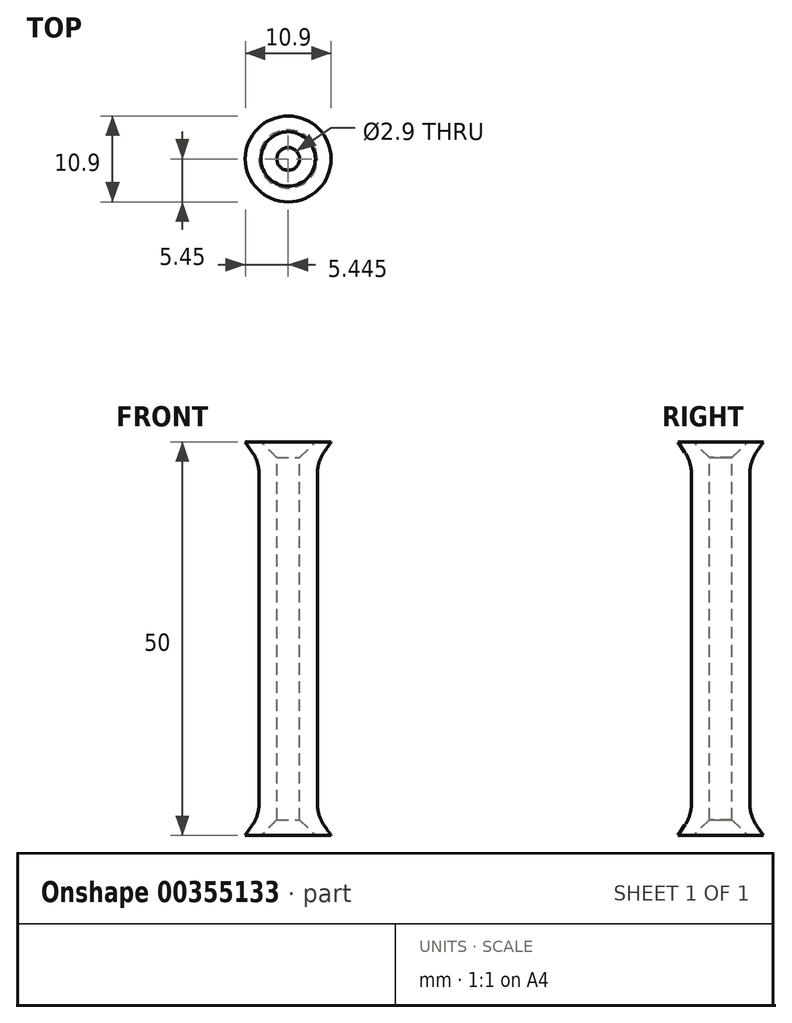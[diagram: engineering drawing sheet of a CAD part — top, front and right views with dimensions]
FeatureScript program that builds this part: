
annotation { "Feature Type Name" : "Feature", "Feature Type Description" : "" }
export const myFeature = defineFeature(function(context is Context, id is Id, definition is map)
    precondition{}
    {
        {
            var Q0;
            Q0=qCreatedBy(makeId("Front.planeOp"),FACE);
            var sketch = newSketch(context, id + "F0", { "sketchPlane" : qUnion([Q0])});
            skLineSegment(sketch, "E0", {"start": v(-17.56, 9.3) * mm, "end": v(-13.56, 9.3) * mm});
            skLineSegment(sketch, "E1", {"start": v(-13.56, 9.3) * mm, "end": v(-13.56, -15.7) * mm});
            skLineSegment(sketch, "E2", {"start": v(-13.56, -15.7) * mm, "end": v(-15.81, -15.7) * mm});
            skLineSegment(sketch, "E3", {"start": v(-15.81, -15.7) * mm, "end": v(-15.81, 6.74) * mm});
            skLineSegment(sketch, "E4", {"start": v(-15.81, 6.74) * mm, "end": v(-17.56, 9.3) * mm});
            skLineSegment(sketch, "E5", {"start": v(-12.11, -9.2) * mm, "end": v(-12.11, -18.1) * mm, "construction": true});
            skLineSegment(sketch, "E6", {"start": v(-13.56, -15.7) * mm, "end": v(-8.34, -15.7) * mm, "construction": true});
            skLineSegment(sketch, "E7.MirrorCS", {"start": v(-13.56, -40.7) * mm, "end": v(-13.56, -15.7) * mm});
            skLineSegment(sketch, "E8.MirrorCS", {"start": v(-15.81, -15.7) * mm, "end": v(-15.81, -38.16) * mm});
            skLineSegment(sketch, "E9.MirrorCS", {"start": v(-17.56, -40.7) * mm, "end": v(-13.56, -40.7) * mm});
            skLineSegment(sketch, "E10.MirrorCS", {"start": v(-15.81, -38.16) * mm, "end": v(-17.56, -40.7) * mm});
            skSolve(sketch);
        }
        {
            var Q0;
            Q0=makeQuery(id+"F0.imprint","IMPRINT",FACE,{"disambiguationData":[TD([[makeQuery(id+"F0.imprint","IMPRINT",EDGE,{"derivedFrom":sQuery(id+"F0.wireOp",EDGE,"E0")}),-1.0]])]});
            var Q1;
            Q1=makeQuery(id+"F0.imprint","IMPRINT",FACE,{"disambiguationData":[TD([[makeQuery(id+"F0.imprint","IMPRINT",EDGE,{"derivedFrom":sQuery(id+"F0.wireOp",EDGE,"E7.MirrorCS")}),1.0]])]});
            var Q2;
            Q2=sQuery(id+"F0.wireOp",EDGE,"E5");
            revolve(context, id + "F1", {"entities" : qUnion([Q0, Q1]), "axis" : qUnion([Q2]), "revolveType" : RevolveType.FULL});
        }
        {
            var Q0;
            Q0=makeQuery(id+"F1.opRevolve","SWEPT_EDGE",EDGE,{"disambiguationData":[OSD([sQuery(id+"F0.wireOp",EDGE,"E3"),sQuery(id+"F0.wireOp",EDGE,"E4")])]});
            var Q1;
            Q1=makeQuery(id+"F1.opRevolve","SWEPT_EDGE",EDGE,{"disambiguationData":[OSD([sQuery(id+"F0.wireOp",EDGE,"E8.MirrorCS"),sQuery(id+"F0.wireOp",EDGE,"E10.MirrorCS")])]});
            fillet(context, id + "F2", {"entities" : qUnion([Q0, Q1]), "radius" : 5 * mm, "tangentPropagation" : true, "allowEdgeOverflow" : false});
        }
        {
            var Q0;
            Q0=makeQuery(id+"F1.opRevolve","SWEPT_EDGE",EDGE,{"disambiguationData":[OSD([sQuery(id+"F0.wireOp",EDGE,"E0"),sQuery(id+"F0.wireOp",EDGE,"E1")])]});
            var Q1;
            Q1=makeQuery(id+"F1.opRevolve","SWEPT_EDGE",EDGE,{"disambiguationData":[OSD([sQuery(id+"F0.wireOp",EDGE,"E7.MirrorCS"),sQuery(id+"F0.wireOp",EDGE,"E9.MirrorCS")])]});
            chamfer(context, id + "F3", {"entities" : qUnion([Q0, Q1]), "chamferType" : ChamferType.OFFSET_ANGLE, "width" : 2 * mm, "oppositeDirection" : false, "angle" : 45 * degree, "tangentPropagation" : true});
        }
    });
